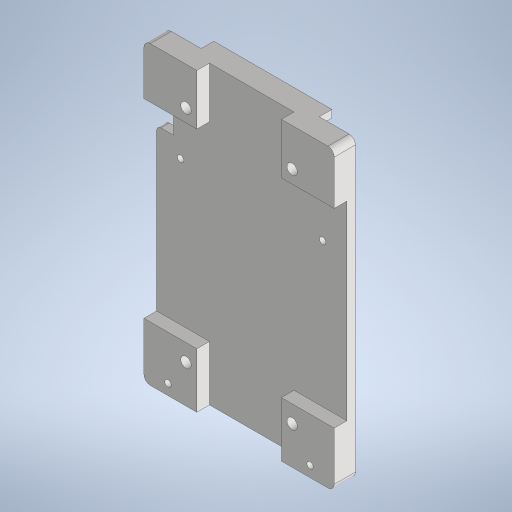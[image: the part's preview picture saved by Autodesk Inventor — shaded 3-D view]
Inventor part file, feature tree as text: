
AUTODESK INVENTOR PART (.ipt)
format: ipt  version: 2023 (Build 270158000, 158)  size: 364,032 bytes
history: native  units: mm
features: sketch x6, extrude x6, projected_geometry x4, other x1, hole x1, fillet x1
ambient origin geometry x8: Origin, YZ Plane, XZ Plane, XY Plane, X Axis, Y Axis, Z Axis, Center Point
bodies: Body1 (feature_tree)
feature tree (19):
  other  "솔리드1"
  sketch  "스케치1"
  extrude  "돌출1"  Depth=45.0mm
  extrude  "돌출2"  Depth=70.0mm
  sketch  "스케치3"
  extrude  "돌출3"  Depth=25.1mm
  extrude  "돌출4"  Depth=52.1mm
  extrude  "돌출6"  Depth=2.5mm
  hole  "구멍3"  [1 undecoded]
  extrude  "돌출7"  Depth=12.0mm
  fillet  "모깎기1"  Radius=13.0mm
  sketch  "스케치4"
  sketch  "스케치5"
  sketch  "스케치7"
  projected_geometry  "투영된 루프4"
  projected_geometry  "투영된 루프5"
  projected_geometry  "투영된 루프6"
  projected_geometry  "투영된 루프7"
  sketch  "스케치9"
note: 1 required parameter value undecoded (feature->parameter linkage not recoverable at this tier; creation-order binding heuristic only, values carry confidence <= 0.55)
